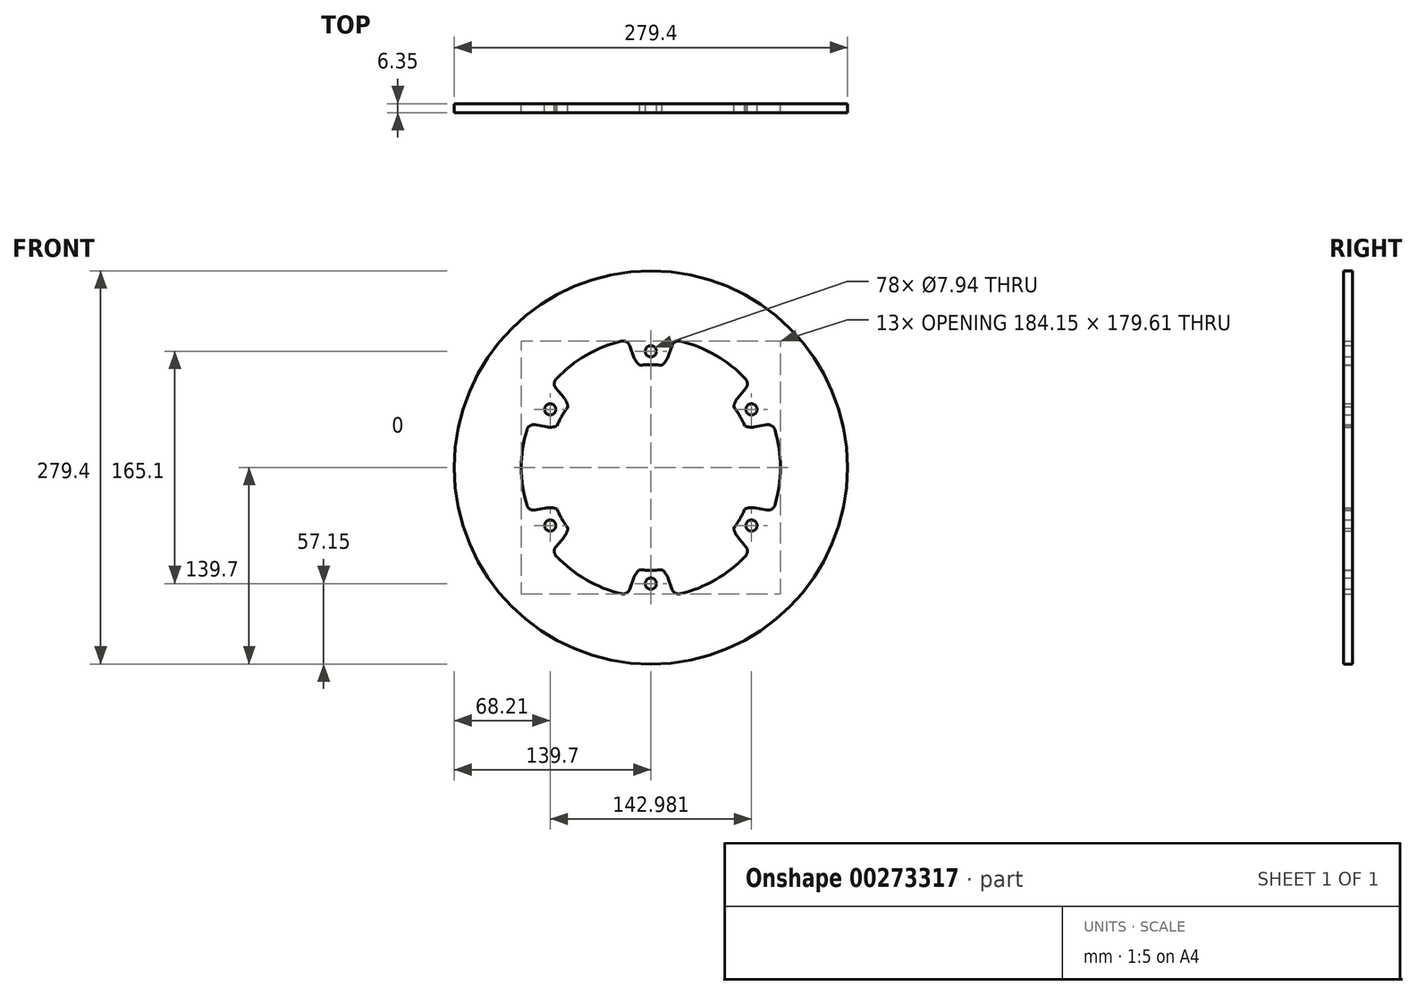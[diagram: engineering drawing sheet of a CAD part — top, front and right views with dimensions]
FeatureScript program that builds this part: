
annotation { "Feature Type Name" : "Feature", "Feature Type Description" : "" }
export const myFeature = defineFeature(function(context is Context, id is Id, definition is map)
    precondition{}
    {
        {
            var Q0;
            Q0=qCreatedBy(makeId("Front.planeOp"),FACE);
            var sketch = newSketch(context, id + "F0", { "sketchPlane" : qUnion([Q0])});
            skCircle(sketch, "E0", {"center": v(0, 0) * mm, "radius": 139.7 * mm});
            skArc(sketch, "E1", {"start": v(-20.87, 89.68) * mm, "mid": v(-46.04, 79.74) * mm, "end": v(-67.23, 62.91) * mm});
            skCircle(sketch, "E2", {"center": v(0, 0) * mm, "radius": 82.55 * mm, "construction": true});
            skLineSegment(sketch, "E3", {"start": v(0, 0) * mm, "end": v(0, 175.08) * mm, "construction": true});
            skLineSegment(sketch, "E4", {"start": v(0, 0) * mm, "end": v(218.94, 0) * mm, "construction": true});
            skLineSegment(sketch, "E5", {"start": v(0, 0) * mm, "end": v(-215.67, 0) * mm, "construction": true});
            skLineSegment(sketch, "E6", {"start": v(0, 0) * mm, "end": v(0, -197.49) * mm, "construction": true});
            skCircle(sketch, "E7", {"center": v(0, 82.55) * mm, "radius": 3.97 * mm});
            skArc(sketch, "E8", {"start": v(-11.93, 78.2) * mm, "mid": v(-10.3, 75.12) * mm, "end": v(-7.89, 72.6) * mm});
            skLineSegment(sketch, "E9", {"start": v(11.93, 78.2) * mm, "end": v(14.94, 86.47) * mm});
            skPoint(sketch, "E10.visualSharp", {"position": v(16.44, 90.6) * mm});
            skArc(sketch, "E10.filletArc", {"start": v(20.87, 89.68) * mm, "mid": v(17.3, 89.2) * mm, "end": v(14.94, 86.47) * mm});
            skArc(sketch, "E11.trimOffspring", {"start": v(7.89, 72.6) * mm, "mid": v(10.3, 75.12) * mm, "end": v(11.93, 78.2) * mm});
            skArc(sketch, "E12.trimOffspring", {"start": v(7.89, 72.6) * mm, "mid": v(0, 73.02) * mm, "end": v(-7.89, 72.6) * mm});
            skArc(sketch, "E13.MirrorCS", {"start": v(-20.87, 89.68) * mm, "mid": v(-17.3, 89.2) * mm, "end": v(-14.94, 86.47) * mm});
            skLineSegment(sketch, "E14.MirrorCS", {"start": v(-11.93, 78.2) * mm, "end": v(-14.94, 86.47) * mm});
            skArc(sketch, "E15.1.0", {"start": v(-88.1, 26.77) * mm, "mid": v(-85.9, 29.62) * mm, "end": v(-82.36, 30.3) * mm});
            skLineSegment(sketch, "E15.1.1", {"start": v(-73.7, 28.77) * mm, "end": v(-82.36, 30.3) * mm});
            skArc(sketch, "E15.1.2", {"start": v(-73.7, 28.77) * mm, "mid": v(-70.2, 28.64) * mm, "end": v(-66.82, 29.47) * mm});
            skArc(sketch, "E15.1.3", {"start": v(-58.93, 43.13) * mm, "mid": v(-63.24, 36.51) * mm, "end": v(-66.82, 29.47) * mm});
            skArc(sketch, "E15.1.4", {"start": v(-58.93, 43.13) * mm, "mid": v(-59.9, 46.48) * mm, "end": v(-61.76, 49.44) * mm});
            skLineSegment(sketch, "E15.1.5", {"start": v(-61.76, 49.44) * mm, "end": v(-67.41, 56.17) * mm});
            skArc(sketch, "E15.1.6", {"start": v(-67.23, 62.91) * mm, "mid": v(-68.6, 59.58) * mm, "end": v(-67.41, 56.17) * mm});
            skArc(sketch, "E15.2.0", {"start": v(-67.23, -62.91) * mm, "mid": v(-68.6, -59.58) * mm, "end": v(-67.41, -56.17) * mm});
            skLineSegment(sketch, "E15.2.1", {"start": v(-61.76, -49.44) * mm, "end": v(-67.41, -56.17) * mm});
            skArc(sketch, "E15.2.2", {"start": v(-61.76, -49.44) * mm, "mid": v(-59.9, -46.48) * mm, "end": v(-58.93, -43.13) * mm});
            skArc(sketch, "E15.2.3", {"start": v(-66.82, -29.47) * mm, "mid": v(-63.24, -36.51) * mm, "end": v(-58.93, -43.13) * mm});
            skArc(sketch, "E15.2.4", {"start": v(-66.82, -29.47) * mm, "mid": v(-70.2, -28.64) * mm, "end": v(-73.7, -28.77) * mm});
            skLineSegment(sketch, "E15.2.5", {"start": v(-73.7, -28.77) * mm, "end": v(-82.36, -30.3) * mm});
            skArc(sketch, "E15.2.6", {"start": v(-88.1, -26.77) * mm, "mid": v(-85.9, -29.62) * mm, "end": v(-82.36, -30.3) * mm});
            skArc(sketch, "E15.3.0", {"start": v(20.87, -89.68) * mm, "mid": v(17.3, -89.2) * mm, "end": v(14.94, -86.47) * mm});
            skLineSegment(sketch, "E15.3.1", {"start": v(11.93, -78.2) * mm, "end": v(14.94, -86.47) * mm});
            skArc(sketch, "E15.3.2", {"start": v(11.93, -78.2) * mm, "mid": v(10.3, -75.12) * mm, "end": v(7.89, -72.6) * mm});
            skArc(sketch, "E15.3.3", {"start": v(-7.89, -72.6) * mm, "mid": v(0, -73.02) * mm, "end": v(7.89, -72.6) * mm});
            skArc(sketch, "E15.3.4", {"start": v(-7.89, -72.6) * mm, "mid": v(-10.3, -75.12) * mm, "end": v(-11.93, -78.2) * mm});
            skLineSegment(sketch, "E15.3.5", {"start": v(-11.93, -78.2) * mm, "end": v(-14.94, -86.47) * mm});
            skArc(sketch, "E15.3.6", {"start": v(-20.87, -89.68) * mm, "mid": v(-17.3, -89.2) * mm, "end": v(-14.94, -86.47) * mm});
            skArc(sketch, "E15.4.0", {"start": v(88.1, -26.77) * mm, "mid": v(85.9, -29.62) * mm, "end": v(82.36, -30.3) * mm});
            skLineSegment(sketch, "E15.4.1", {"start": v(73.7, -28.77) * mm, "end": v(82.36, -30.3) * mm});
            skArc(sketch, "E15.4.2", {"start": v(73.7, -28.77) * mm, "mid": v(70.2, -28.64) * mm, "end": v(66.82, -29.47) * mm});
            skArc(sketch, "E15.4.3", {"start": v(58.93, -43.13) * mm, "mid": v(63.24, -36.51) * mm, "end": v(66.82, -29.47) * mm});
            skArc(sketch, "E15.4.4", {"start": v(58.93, -43.13) * mm, "mid": v(59.9, -46.48) * mm, "end": v(61.76, -49.44) * mm});
            skLineSegment(sketch, "E15.4.5", {"start": v(61.76, -49.44) * mm, "end": v(67.41, -56.17) * mm});
            skArc(sketch, "E15.4.6", {"start": v(67.23, -62.91) * mm, "mid": v(68.6, -59.58) * mm, "end": v(67.41, -56.17) * mm});
            skArc(sketch, "E15.5.0", {"start": v(67.23, 62.91) * mm, "mid": v(68.6, 59.58) * mm, "end": v(67.41, 56.17) * mm});
            skLineSegment(sketch, "E15.5.1", {"start": v(61.76, 49.44) * mm, "end": v(67.41, 56.17) * mm});
            skArc(sketch, "E15.5.2", {"start": v(61.76, 49.44) * mm, "mid": v(59.9, 46.48) * mm, "end": v(58.93, 43.13) * mm});
            skArc(sketch, "E15.5.3", {"start": v(66.82, 29.47) * mm, "mid": v(63.24, 36.51) * mm, "end": v(58.93, 43.13) * mm});
            skArc(sketch, "E15.5.4", {"start": v(66.82, 29.47) * mm, "mid": v(70.2, 28.64) * mm, "end": v(73.7, 28.77) * mm});
            skLineSegment(sketch, "E15.5.5", {"start": v(73.7, 28.77) * mm, "end": v(82.36, 30.3) * mm});
            skArc(sketch, "E15.5.6", {"start": v(88.1, 26.77) * mm, "mid": v(85.9, 29.62) * mm, "end": v(82.36, 30.3) * mm});
            skCircle(sketch, "E16.1.0", {"center": v(-71.5, -41.27) * mm, "radius": 3.97 * mm, "construction": true});
            skCircle(sketch, "E16.2.0", {"center": v(71.5, -41.28) * mm, "radius": 3.97 * mm, "construction": true});
            skCircle(sketch, "E17.1.0", {"center": v(-71.5, 41.28) * mm, "radius": 3.97 * mm});
            skCircle(sketch, "E17.2.0", {"center": v(-71.5, -41.27) * mm, "radius": 3.97 * mm});
            skCircle(sketch, "E17.3.0", {"center": v(0, -82.55) * mm, "radius": 3.97 * mm});
            skCircle(sketch, "E17.4.0", {"center": v(71.5, -41.28) * mm, "radius": 3.97 * mm});
            skCircle(sketch, "E17.5.0", {"center": v(71.5, 41.28) * mm, "radius": 3.97 * mm});
            skArc(sketch, "E18.trimOffspring", {"start": v(-88.1, 26.77) * mm, "mid": v(-92.08, 0) * mm, "end": v(-88.1, -26.77) * mm});
            skArc(sketch, "E19.trimOffspring", {"start": v(67.23, 62.91) * mm, "mid": v(46.04, 79.74) * mm, "end": v(20.87, 89.68) * mm});
            skArc(sketch, "E20.trimOffspring", {"start": v(88.1, -26.77) * mm, "mid": v(92.08, 0) * mm, "end": v(88.1, 26.77) * mm});
            skArc(sketch, "E21.trimOffspring", {"start": v(-67.23, -62.91) * mm, "mid": v(-46.04, -79.74) * mm, "end": v(-20.87, -89.68) * mm});
            skArc(sketch, "E22.trimOffspring", {"start": v(20.87, -89.68) * mm, "mid": v(46.04, -79.74) * mm, "end": v(67.23, -62.91) * mm});
            skSolve(sketch);
        }
        {
            var Q0;
            Q0 = qSketchRegion(id + "F0", true);
            extrude(context, id + "F1", {"entities" : qUnion([Q0]), "depth" : 6.35 * mm});
        }
    });
